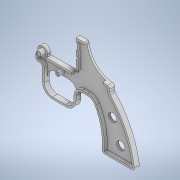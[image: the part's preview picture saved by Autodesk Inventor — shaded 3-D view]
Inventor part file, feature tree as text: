
AUTODESK INVENTOR PART (.ipt)
format: ipt  version: 2021 (Build 250183000, 183)  size: 357,888 bytes
history: native  units: in
note: dims shown in document units (in); Inventor stores cm internally (conversion verified against a paired STEP export)
features: sketch x9, extrude x8, fillet x2, plane x1, revolve x1
ambient origin geometry x8: Origin, YZ Plane, XZ Plane, XY Plane, X Axis, Y Axis, Z Axis, Center Point
bodies: Solid1 (feature_tree)
feature tree (21):
  extrude  "Extrusion1"  Depth=0.1378in TaperAngle=0.0deg
  extrude  "Extrusion2"  Depth=0.0787in TaperAngle=0.0deg
  extrude  "Extrusion3"  Depth=0.0984in TaperAngle=0.0deg
  extrude  "Extrusion4"  Depth=0.1575in TaperAngle=0.0deg
  extrude  "Extrusion5"  Depth=0.7087in
  extrude  "Extrusion6"  Depth=0.5709in
  fillet  "Fillet1"  Radius=0.3937in
  fillet  "Fillet2"  Radius=1.4173in
  plane  "Work Plane1"
  revolve  "Revolution1"  [1 undecoded]
  extrude  "Extrusion7"  Depth=0.5709in TaperAngle=0.0deg
  extrude  "Extrusion8"  Depth=0.5709in TaperAngle=0.0deg
  sketch  "Sketch1"  dims[d0=0.0984in d1=0.0in d2=0.1378in d3=0.0in]
  sketch  "Sketch2"  dims[d4=0.0394in d5=0.0in d6=0.0787in d7=0.0in]
  sketch  "Sketch3"  dims[d8=2.2662in d9=0.0in d10=0.0984in d11=0.0in]
  sketch  "Sketch4"  dims[d12=0.0197in d13=0.1575in d14=0.0in]
  sketch  "Sketch6"  dims[d15=0.0197in d16=0.7087in]
  sketch  "Sketch7"  dims[d23=0.3937in d24=0.5709in d25=0.3937in d26=1.4173in]
  sketch  "Sketch11"  dims[d27=0.0262in d28=0.5709in]
  sketch  "Sketch12"  dims[d29=180.0deg]
  sketch  "Sketch13"  dims[d30=0.3937in d31=0.5709in d32=0.3937in d33=1.4173in d34=0.0262in d35=0.5709in d36=1.8937in d37=0.0in d38=0.0262in d39=0.0in]
note: 1 required parameter value undecoded (feature->parameter linkage not recoverable at this tier; creation-order binding heuristic only, values carry confidence <= 0.55)
